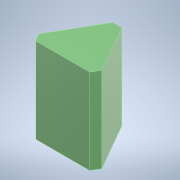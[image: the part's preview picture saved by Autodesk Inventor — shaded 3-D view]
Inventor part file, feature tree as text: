
AUTODESK INVENTOR PART (.ipt)
format: ipt  version: 2021 (Build 250183000, 183)  size: 108,544 bytes
history: native  units: mm
features: extrude x1, sketch x1
ambient origin geometry x8: Origin, YZ Plane, XZ Plane, XY Plane, X Axis, Y Axis, Z Axis, Center Point
bodies: Solid1 (feature_tree)
feature tree (2):
  extrude  "Extrusion1"  Depth=30.6mm
  sketch  "Sketch1"  dims[d0=19.6mm d1=3.2mm d2=30.6mm d3=0.0mm d4=14.914188mm]
